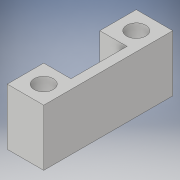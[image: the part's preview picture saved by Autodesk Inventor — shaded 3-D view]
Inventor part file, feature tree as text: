
AUTODESK INVENTOR PART (.ipt)
format: ipt  version: 2019 (Build 230136000, 136)  size: 104,448 bytes
history: native  units: in
note: dims shown in document units (in); Inventor stores cm internally (conversion verified against a paired STEP export)
features: extrude x1, sketch x1
ambient origin geometry x8: Origin, YZ Plane, XZ Plane, XY Plane, X Axis, Y Axis, Z Axis, Center Point
bodies: Solid1 (feature_tree)
feature tree (2):
  extrude  "Extrusion1"  Depth=1.2205in
  sketch  "Sketch1"  dims[d1=0.4134in d2=0.4134in d3=2.0in d4=0.394in d5=0.394in d6=0.394in d7=0.2in d8=0.394in d9=0.394in d10=0.394in d11=0.394in d12=1.2205in d13=0.0in]
